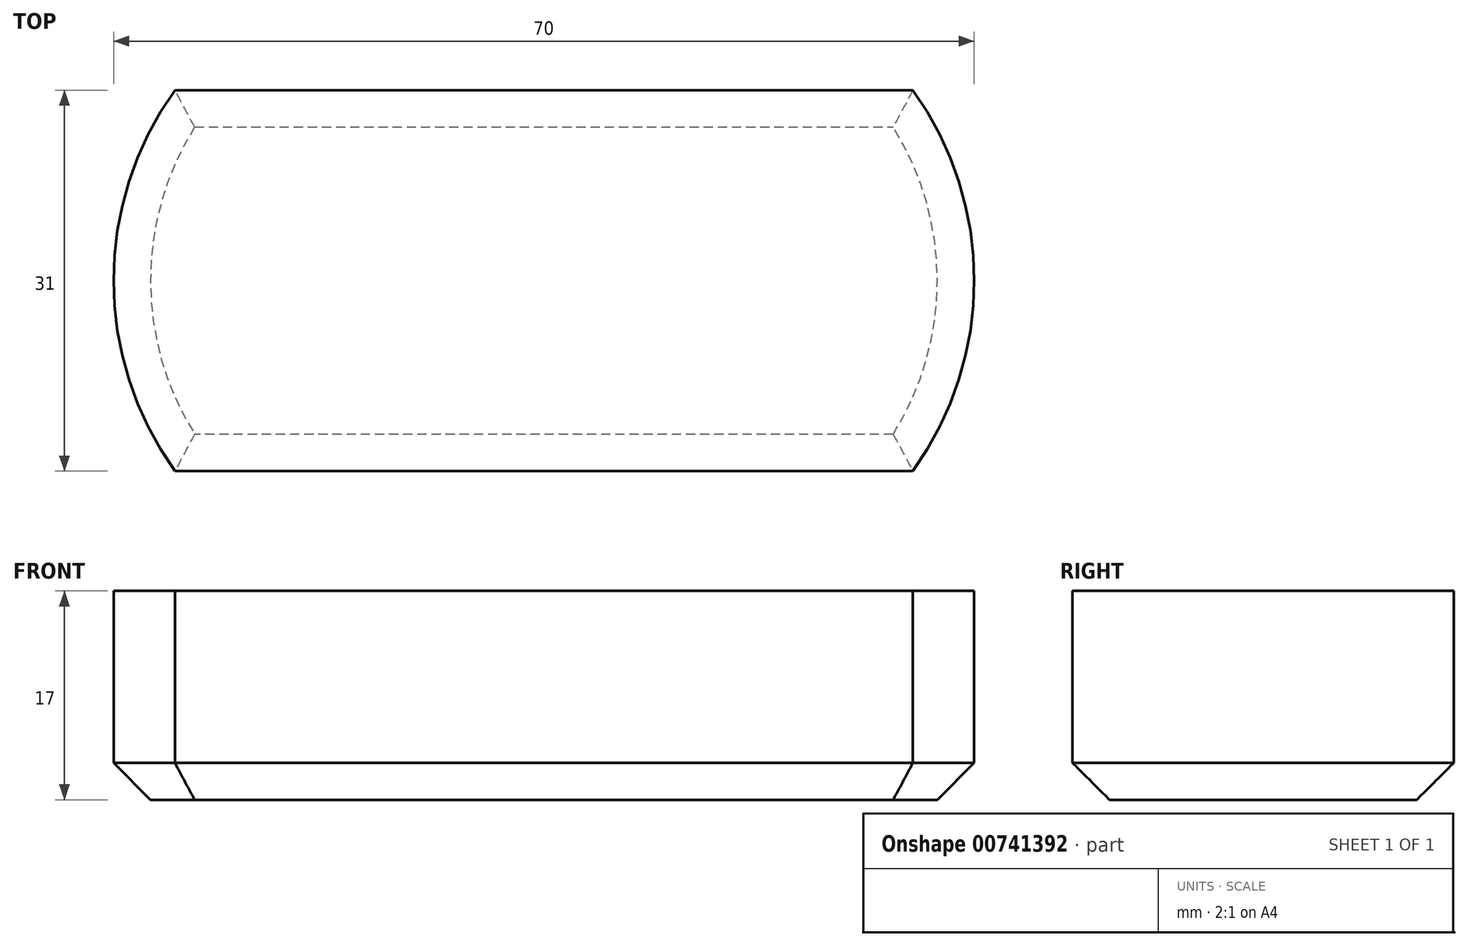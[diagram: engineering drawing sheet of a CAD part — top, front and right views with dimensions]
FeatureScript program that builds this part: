
annotation { "Feature Type Name" : "Feature", "Feature Type Description" : "" }
export const myFeature = defineFeature(function(context is Context, id is Id, definition is map)
    precondition{}
    {
        {
            var Q0;
            Q0=qCreatedBy(makeId("Top.planeOp"),FACE);
            var sketch = newSketch(context, id + "F0", { "sketchPlane" : qUnion([Q0])});
            skLineSegment(sketch, "E0.bottom", {"start": v(-30, -15.5) * mm, "end": v(30, -15.5) * mm});
            skLineSegment(sketch, "E0.top", {"start": v(-30, 15.5) * mm, "end": v(30, 15.5) * mm});
            skLineSegment(sketch, "E0.left", {"start": v(-30, -15.5) * mm, "end": v(-30, 15.5) * mm});
            skLineSegment(sketch, "E0.right", {"start": v(30, -15.5) * mm, "end": v(30, 15.5) * mm});
            skPoint(sketch, "E0.middle", {"position": v(0, 0) * mm});
            skArc(sketch, "E1", {"start": v(-30, 15.5) * mm, "mid": v(-35, 0) * mm, "end": v(-30, -15.5) * mm});
            skArc(sketch, "E2", {"start": v(30, -15.5) * mm, "mid": v(35, 0) * mm, "end": v(30, 15.5) * mm});
            skSolve(sketch);
        }
        {
            var Q0;
            Q0 = qSketchRegion(id + "F0", true);
            extrude(context, id + "F1", {"entities" : qUnion([Q0]), "depth" : 17 * mm, "offsetDistance" : 25.4 * mm});
        }
        {
            var Q0;
            Q0=makeQuery(id+"F1.opExtrude","CAP_FACE",FACE,{"disambiguationData":[OSD([sQuery(id+"F0.wireOp",EDGE,"E0.bottom"),sQuery(id+"F0.wireOp",EDGE,"E0.top"),sQuery(id+"F0.wireOp",EDGE,"E1"),sQuery(id+"F0.wireOp",EDGE,"E2")])],"isStart":true});
            chamfer(context, id + "F2", {"entities" : qUnion([Q0]), "width" : 3 * mm, "tangentPropagation" : true});
        }
    });
